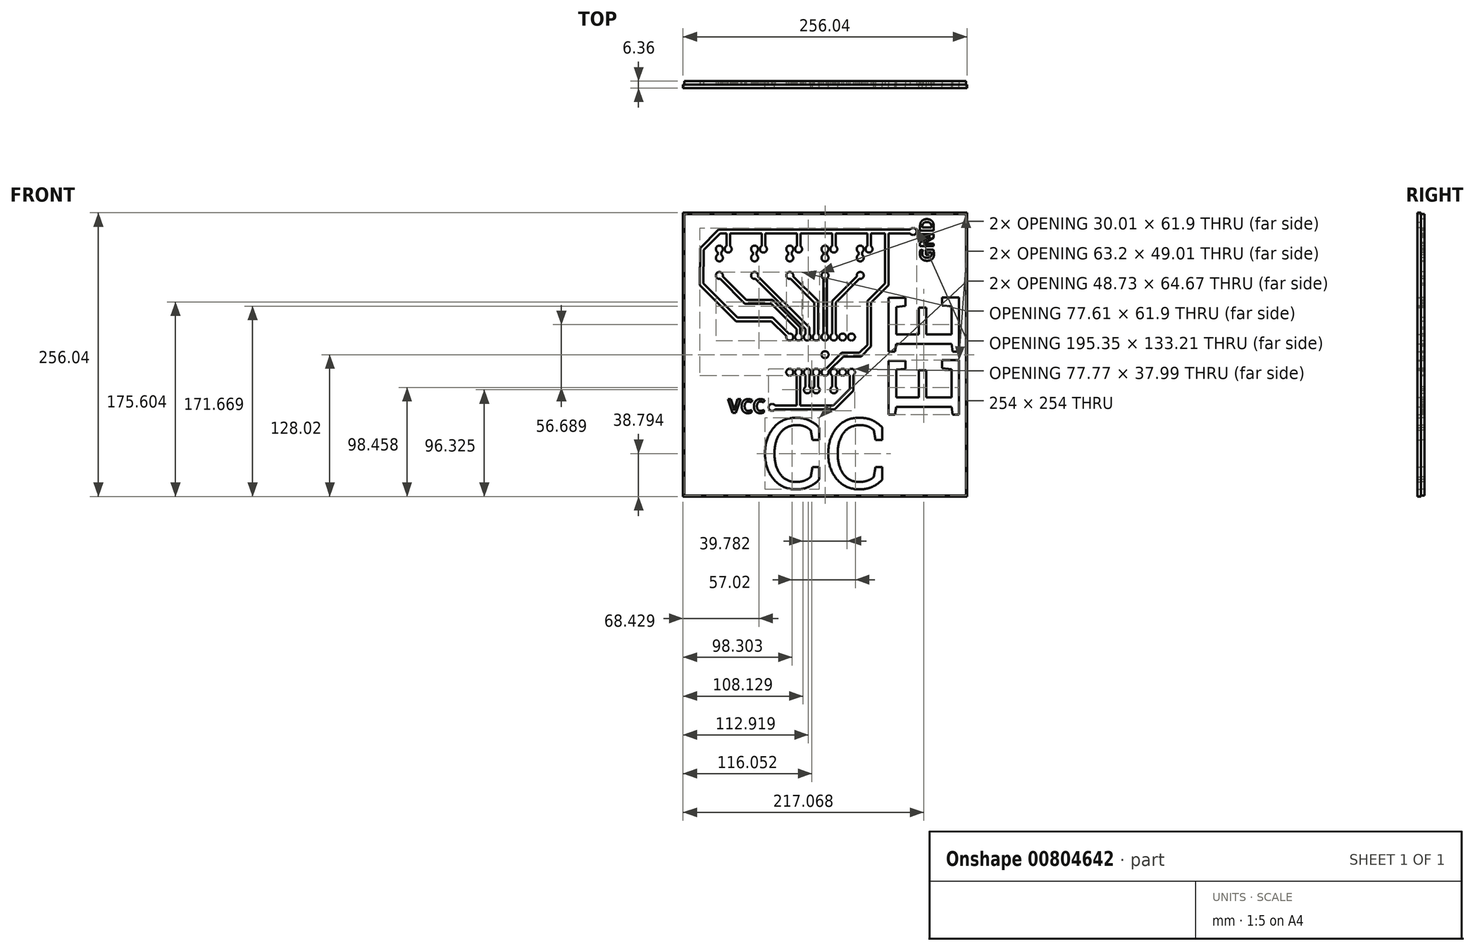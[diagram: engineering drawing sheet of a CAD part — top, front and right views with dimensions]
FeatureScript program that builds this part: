
annotation { "Feature Type Name" : "Feature", "Feature Type Description" : "" }
export const myFeature = defineFeature(function(context is Context, id is Id, definition is map)
    precondition{}
    {
        {
            var Q0;
            Q0=qCreatedBy(makeId("Front.planeOp"),FACE);
            var sketch = newSketch(context, id + "F0", { "sketchPlane" : qUnion([Q0])});
            skLineSegment(sketch, "E0.bottom", {"start": v(127, 127) * mm, "end": v(-127, 127) * mm});
            skLineSegment(sketch, "E0.top", {"start": v(127, -127) * mm, "end": v(-127, -127) * mm});
            skLineSegment(sketch, "E0.left", {"start": v(127, 127) * mm, "end": v(127, -127) * mm});
            skLineSegment(sketch, "E0.right", {"start": v(-127, 127) * mm, "end": v(-127, -127) * mm});
            skPoint(sketch, "E0.middle", {"position": v(0, 0) * mm});
            skText(sketch, "E1", { "text": "CC", "fontName": "RobotoSlab-Regular.ttf"});
            skText(sketch, "E2", { "text": "EE", "fontName": "RobotoSlab-Regular.ttf"});
            skText(sketch, "E3", { "text": "TOP", "fontName": "OpenSans-Regular.ttf"});
            skCircle(sketch, "E4", {"center": v(0, 0) * mm, "radius": 3.18 * mm});
            skLineSegment(sketch, "E5.0", {"start": v(128.02, -128.02) * mm, "end": v(-128.02, -128.02) * mm});
            skLineSegment(sketch, "E5.1", {"start": v(128.02, 128.02) * mm, "end": v(128.02, -128.02) * mm});
            skLineSegment(sketch, "E5.2", {"start": v(128.02, 128.02) * mm, "end": v(-128.02, 128.02) * mm});
            skLineSegment(sketch, "E5.3", {"start": v(-128.02, 128.02) * mm, "end": v(-128.02, -128.02) * mm});
            skPoint(sketch, "E6", {"position": v(0, 15.88) * mm});
            skPoint(sketch, "E7", {"position": v(0, -15.88) * mm});
            skPoint(sketch, "E8", {"position": v(7.95, -15.88) * mm});
            skPoint(sketch, "E9", {"position": v(15.9, -15.88) * mm});
            skPoint(sketch, "E10", {"position": v(23.85, -15.88) * mm});
            skPoint(sketch, "E11", {"position": v(-7.95, -15.88) * mm});
            skPoint(sketch, "E12", {"position": v(-15.9, -15.88) * mm});
            skPoint(sketch, "E13", {"position": v(-23.85, -15.88) * mm});
            skPoint(sketch, "E14", {"position": v(-31.8, -15.88) * mm});
            skPoint(sketch, "E15", {"position": v(7.95, 15.88) * mm});
            skPoint(sketch, "E16", {"position": v(15.9, 15.88) * mm});
            skPoint(sketch, "E17", {"position": v(23.85, 15.88) * mm});
            skPoint(sketch, "E18", {"position": v(-7.95, 15.88) * mm});
            skPoint(sketch, "E19", {"position": v(-15.9, 15.88) * mm});
            skPoint(sketch, "E20", {"position": v(-23.85, 15.88) * mm});
            skPoint(sketch, "E21", {"position": v(-31.8, 15.88) * mm});
            skPoint(sketch, "E22", {"position": v(-15.9, -31.75) * mm});
            skPoint(sketch, "E23", {"position": v(-7.95, -31.75) * mm});
            skPoint(sketch, "E24", {"position": v(7.95, -31.75) * mm});
            skPoint(sketch, "E25", {"position": v(-47.68, -47.62) * mm});
            skPoint(sketch, "E26", {"position": v(0, 71.45) * mm});
            skPoint(sketch, "E27", {"position": v(31.75, 71.45) * mm});
            skPoint(sketch, "E28", {"position": v(-31.75, 71.45) * mm});
            skPoint(sketch, "E29", {"position": v(-63.5, 71.45) * mm});
            skPoint(sketch, "E30", {"position": v(-95.25, 71.45) * mm});
            skArc(sketch, "E31", {"start": v(-34.87, 16.68) * mm, "mid": v(-29.56, 13.63) * mm, "end": v(-32.6, 18.95) * mm});
            skArc(sketch, "E32", {"start": v(-24.98, 18.84) * mm, "mid": v(-24.11, 12.71) * mm, "end": v(-22.25, 18.62) * mm});
            skArc(sketch, "E33", {"start": v(-17.5, 18.62) * mm, "mid": v(-15.9, 12.7) * mm, "end": v(-14.3, 18.62) * mm});
            skArc(sketch, "E34", {"start": v(-9.55, 18.62) * mm, "mid": v(-7.95, 12.7) * mm, "end": v(-6.35, 18.62) * mm});
            skArc(sketch, "E35", {"start": v(-1.6, 18.62) * mm, "mid": v(0, 12.7) * mm, "end": v(1.6, 18.62) * mm});
            skArc(sketch, "E36", {"start": v(6.35, 18.62) * mm, "mid": v(7.95, 12.7) * mm, "end": v(9.55, 18.62) * mm});
            skCircle(sketch, "E37", {"center": v(15.9, 15.88) * mm, "radius": 3.18 * mm});
            skCircle(sketch, "E38", {"center": v(23.85, 15.88) * mm, "radius": 3.18 * mm});
            skCircle(sketch, "E39", {"center": v(-31.8, -15.88) * mm, "radius": 3.18 * mm});
            skArc(sketch, "E40", {"start": v(-22.25, -18.62) * mm, "mid": v(-24.68, -12.81) * mm, "end": v(-23.85, -19.05) * mm});
            skArc(sketch, "E41", {"start": v(-15.9, -19.05) * mm, "mid": v(-15.07, -12.81) * mm, "end": v(-17.5, -18.62) * mm});
            skArc(sketch, "E42", {"start": v(-6.35, -18.62) * mm, "mid": v(-7.95, -12.7) * mm, "end": v(-9.55, -18.62) * mm});
            skArc(sketch, "E43", {"start": v(0.8, -12.8) * mm, "mid": v(-2.24, -18.12) * mm, "end": v(3.07, -15.07) * mm});
            skArc(sketch, "E44", {"start": v(9.55, -18.62) * mm, "mid": v(7.95, -12.7) * mm, "end": v(6.35, -18.62) * mm});
            skCircle(sketch, "E45", {"center": v(15.9, -15.88) * mm, "radius": 3.18 * mm});
            skArc(sketch, "E46", {"start": v(25.45, -18.62) * mm, "mid": v(23.85, -12.7) * mm, "end": v(22.25, -18.62) * mm});
            skArc(sketch, "E47", {"start": v(30.94, 68.38) * mm, "mid": v(34, 73.7) * mm, "end": v(28.68, 70.64) * mm});
            skArc(sketch, "E48", {"start": v(1.6, 68.7) * mm, "mid": v(0, 74.63) * mm, "end": v(-1.6, 68.7) * mm});
            skArc(sketch, "E49", {"start": v(-28.68, 70.64) * mm, "mid": v(-34, 73.7) * mm, "end": v(-30.94, 68.38) * mm});
            skArc(sketch, "E50", {"start": v(-60.43, 70.64) * mm, "mid": v(-65.74, 73.7) * mm, "end": v(-62.7, 68.38) * mm});
            skArc(sketch, "E51", {"start": v(-92.18, 70.64) * mm, "mid": v(-97.5, 73.7) * mm, "end": v(-94.45, 68.38) * mm});
            skPoint(sketch, "E52", {"position": v(7.95, 47.62) * mm});
            skPoint(sketch, "E53", {"position": v(-7.95, 47.62) * mm});
            skPoint(sketch, "E54", {"position": v(-15.9, 23.83) * mm});
            skPoint(sketch, "E55", {"position": v(-23.85, 23.83) * mm});
            skPoint(sketch, "E56", {"position": v(-47.68, 47.62) * mm});
            skPoint(sketch, "E57", {"position": v(-71.5, 47.62) * mm});
            skPoint(sketch, "E58", {"position": v(-47.68, 31.75) * mm});
            skPoint(sketch, "E59", {"position": v(-79.43, 31.75) * mm});
            skPoint(sketch, "E60", {"position": v(-111.12, 95.25) * mm});
            skPoint(sketch, "E61", {"position": v(-111.18, 63.5) * mm});
            skPoint(sketch, "E62", {"position": v(-95.25, 95.25) * mm});
            skPoint(sketch, "E63", {"position": v(-87.3, 95.25) * mm});
            skPoint(sketch, "E64", {"position": v(-63.5, 95.25) * mm});
            skPoint(sketch, "E65", {"position": v(-55.55, 95.25) * mm});
            skPoint(sketch, "E66", {"position": v(-31.75, 95.25) * mm});
            skPoint(sketch, "E67", {"position": v(-23.8, 95.25) * mm});
            skPoint(sketch, "E68", {"position": v(0, 95.25) * mm});
            skPoint(sketch, "E69", {"position": v(31.75, 95.25) * mm});
            skPoint(sketch, "E70", {"position": v(7.95, 95.25) * mm});
            skPoint(sketch, "E71", {"position": v(39.7, 95.25) * mm});
            skPoint(sketch, "E72", {"position": v(-95.25, 87.3) * mm});
            skPoint(sketch, "E73", {"position": v(-63.5, 87.3) * mm});
            skPoint(sketch, "E74", {"position": v(-31.75, 87.3) * mm});
            skPoint(sketch, "E75", {"position": v(0, 87.3) * mm});
            skPoint(sketch, "E76", {"position": v(31.75, 87.3) * mm});
            skPoint(sketch, "E77", {"position": v(-95.25, 111.12) * mm});
            skPoint(sketch, "E78", {"position": v(55.58, 111.12) * mm});
            skArc(sketch, "E79", {"start": v(-96.85, 90.04) * mm, "mid": v(-95.25, 84.12) * mm, "end": v(-93.65, 90.04) * mm});
            skArc(sketch, "E80", {"start": v(-93.65, 92.5) * mm, "mid": v(-95.25, 98.42) * mm, "end": v(-96.85, 92.5) * mm});
            skArc(sketch, "E81", {"start": v(-88.9, 98) * mm, "mid": v(-87.3, 92.07) * mm, "end": v(-85.7, 98) * mm});
            skArc(sketch, "E82", {"start": v(-61.9, 92.5) * mm, "mid": v(-63.5, 98.42) * mm, "end": v(-65.1, 92.5) * mm});
            skArc(sketch, "E83", {"start": v(-65.1, 90.04) * mm, "mid": v(-63.5, 84.12) * mm, "end": v(-61.9, 90.04) * mm});
            skArc(sketch, "E84", {"start": v(-33.35, 90.04) * mm, "mid": v(-31.75, 84.12) * mm, "end": v(-30.15, 90.04) * mm});
            skArc(sketch, "E85", {"start": v(-57.15, 98) * mm, "mid": v(-55.55, 92.07) * mm, "end": v(-53.95, 98) * mm});
            skArc(sketch, "E86", {"start": v(-30.15, 92.5) * mm, "mid": v(-31.75, 98.42) * mm, "end": v(-33.35, 92.5) * mm});
            skArc(sketch, "E87", {"start": v(-25.4, 98) * mm, "mid": v(-23.8, 92.07) * mm, "end": v(-22.2, 98) * mm});
            skArc(sketch, "E88", {"start": v(-1.6, 90.04) * mm, "mid": v(0, 84.12) * mm, "end": v(1.6, 90.04) * mm});
            skArc(sketch, "E89", {"start": v(1.6, 92.5) * mm, "mid": v(0, 98.42) * mm, "end": v(-1.6, 92.5) * mm});
            skArc(sketch, "E90", {"start": v(6.35, 98) * mm, "mid": v(7.95, 92.07) * mm, "end": v(9.55, 98) * mm});
            skArc(sketch, "E91", {"start": v(30.15, 90.04) * mm, "mid": v(31.75, 84.12) * mm, "end": v(33.35, 90.04) * mm});
            skArc(sketch, "E92", {"start": v(33.35, 92.5) * mm, "mid": v(31.75, 98.42) * mm, "end": v(30.15, 92.5) * mm});
            skArc(sketch, "E93", {"start": v(38.1, 98) * mm, "mid": v(39.7, 92.07) * mm, "end": v(41.3, 98) * mm});
            skArc(sketch, "E94", {"start": v(76.66, 109.52) * mm, "mid": v(82.58, 111.12) * mm, "end": v(76.66, 112.73) * mm});
            skArc(sketch, "E95", {"start": v(6.35, -29) * mm, "mid": v(7.95, -34.92) * mm, "end": v(9.55, -29) * mm});
            skArc(sketch, "E96", {"start": v(-7.95, -28.57) * mm, "mid": v(-8.78, -34.81) * mm, "end": v(-6.35, -29) * mm});
            skArc(sketch, "E97", {"start": v(-17.5, -29) * mm, "mid": v(-15.9, -34.92) * mm, "end": v(-14.3, -29) * mm});
            skPoint(sketch, "E98", {"position": v(7.95, -47.62) * mm});
            skPoint(sketch, "E99", {"position": v(23.85, -31.75) * mm});
            skLineSegment(sketch, "E100.0", {"start": v(-95.91, 112.73) * mm, "end": v(79.4, 112.73) * mm});
            skLineSegment(sketch, "E100.1", {"start": v(-95.91, 112.73) * mm, "end": v(-112.72, 95.91) * mm});
            skLineSegment(sketch, "E100.2", {"start": v(-32.93, 14.74) * mm, "end": v(-48.34, 30.15) * mm});
            skLineSegment(sketch, "E100.3", {"start": v(-48.34, 30.15) * mm, "end": v(-80.09, 30.15) * mm});
            skLineSegment(sketch, "E100.4", {"start": v(-80.09, 30.15) * mm, "end": v(-112.78, 62.84) * mm});
            skLineSegment(sketch, "E100.5", {"start": v(-112.78, 62.84) * mm, "end": v(-112.72, 95.91) * mm});
            skLineSegment(sketch, "E101.0", {"start": v(-72.17, 46.02) * mm, "end": v(-96.38, 70.32) * mm});
            skLineSegment(sketch, "E101.1", {"start": v(-48.34, 46.02) * mm, "end": v(-72.17, 46.02) * mm});
            skLineSegment(sketch, "E101.2", {"start": v(-24.98, 22.7) * mm, "end": v(-48.34, 46.02) * mm});
            skLineSegment(sketch, "E102.0", {"start": v(-17.5, 23.16) * mm, "end": v(-64.63, 70.32) * mm});
            skLineSegment(sketch, "E102.1", {"start": v(-17.5, 15.88) * mm, "end": v(-17.5, 23.16) * mm});
            skLineSegment(sketch, "E103.0", {"start": v(-14.3, 24.49) * mm, "end": v(-62.37, 72.58) * mm});
            skLineSegment(sketch, "E103.1", {"start": v(-14.3, 15.87) * mm, "end": v(-14.3, 24.49) * mm});
            skLineSegment(sketch, "E104.0", {"start": v(-70.84, 49.23) * mm, "end": v(-94.12, 72.58) * mm});
            skLineSegment(sketch, "E104.1", {"start": v(-47.01, 49.23) * mm, "end": v(-70.84, 49.23) * mm});
            skLineSegment(sketch, "E104.2", {"start": v(-22.25, 24.49) * mm, "end": v(-47.01, 49.23) * mm});
            skLineSegment(sketch, "E104.3", {"start": v(-22.25, 24.49) * mm, "end": v(-22.25, 15.88) * mm});
            skLineSegment(sketch, "E105.0", {"start": v(-94.59, 109.52) * mm, "end": v(-88.9, 109.52) * mm});
            skLineSegment(sketch, "E105.1", {"start": v(-94.59, 109.52) * mm, "end": v(-109.53, 94.59) * mm});
            skLineSegment(sketch, "E105.2", {"start": v(-30.67, 17) * mm, "end": v(-47.01, 33.35) * mm});
            skLineSegment(sketch, "E105.3", {"start": v(-47.01, 33.35) * mm, "end": v(-78.76, 33.35) * mm});
            skLineSegment(sketch, "E105.4", {"start": v(-78.76, 33.35) * mm, "end": v(-109.57, 64.16) * mm});
            skLineSegment(sketch, "E105.5", {"start": v(-109.57, 64.16) * mm, "end": v(-109.53, 94.59) * mm});
            skLineSegment(sketch, "E106.0", {"start": v(1.13, -17) * mm, "end": v(16.52, -1.6) * mm});
            skLineSegment(sketch, "E106.1", {"start": v(16.52, -1.6) * mm, "end": v(32.4, -1.6) * mm});
            skLineSegment(sketch, "E106.2", {"start": v(57.18, 111.12) * mm, "end": v(57.18, 62.84) * mm});
            skLineSegment(sketch, "E106.3", {"start": v(57.18, 62.84) * mm, "end": v(41.3, 46.95) * mm});
            skLineSegment(sketch, "E106.4", {"start": v(41.3, 46.95) * mm, "end": v(41.3, 7.31) * mm});
            skLineSegment(sketch, "E106.5", {"start": v(32.4, -1.6) * mm, "end": v(41.3, 7.31) * mm});
            skLineSegment(sketch, "E107.0", {"start": v(-1.13, -14.74) * mm, "end": v(15.2, 1.6) * mm});
            skLineSegment(sketch, "E107.1", {"start": v(15.2, 1.6) * mm, "end": v(31.07, 1.6) * mm});
            skLineSegment(sketch, "E107.2", {"start": v(53.97, 111.12) * mm, "end": v(53.97, 64.16) * mm});
            skLineSegment(sketch, "E107.3", {"start": v(53.97, 64.16) * mm, "end": v(38.1, 48.27) * mm});
            skLineSegment(sketch, "E107.4", {"start": v(38.1, 48.27) * mm, "end": v(38.1, 8.64) * mm});
            skLineSegment(sketch, "E107.5", {"start": v(31.07, 1.6) * mm, "end": v(38.1, 8.64) * mm});
            skLineSegment(sketch, "E108.0", {"start": v(38.1, 95.25) * mm, "end": v(38.1, 111.12) * mm});
            skLineSegment(sketch, "E109.0", {"start": v(41.3, 95.25) * mm, "end": v(41.3, 111.12) * mm});
            skLineSegment(sketch, "E110.0", {"start": v(9.55, 95.25) * mm, "end": v(9.55, 111.12) * mm});
            skLineSegment(sketch, "E111.0", {"start": v(6.35, 95.25) * mm, "end": v(6.35, 111.12) * mm});
            skLineSegment(sketch, "E112.0", {"start": v(1.6, 95.25) * mm, "end": v(1.6, 87.3) * mm});
            skLineSegment(sketch, "E113.0", {"start": v(-1.6, 95.25) * mm, "end": v(-1.6, 87.3) * mm});
            skLineSegment(sketch, "E114.0", {"start": v(-22.2, 95.25) * mm, "end": v(-22.2, 111.12) * mm});
            skLineSegment(sketch, "E115.0", {"start": v(-25.4, 95.25) * mm, "end": v(-25.4, 111.12) * mm});
            skLineSegment(sketch, "E116.0", {"start": v(-53.95, 95.25) * mm, "end": v(-53.95, 111.12) * mm});
            skLineSegment(sketch, "E117.0", {"start": v(-85.7, 95.25) * mm, "end": v(-85.7, 111.12) * mm});
            skLineSegment(sketch, "E118.0", {"start": v(-57.15, 95.25) * mm, "end": v(-57.15, 111.12) * mm});
            skLineSegment(sketch, "E119.0", {"start": v(-30.15, 87.3) * mm, "end": v(-30.15, 95.25) * mm});
            skLineSegment(sketch, "E120.0", {"start": v(-33.35, 87.3) * mm, "end": v(-33.35, 95.25) * mm});
            skLineSegment(sketch, "E121.0", {"start": v(-88.9, 95.25) * mm, "end": v(-88.9, 111.12) * mm});
            skLineSegment(sketch, "E122.0", {"start": v(-9.55, 46.96) * mm, "end": v(-32.88, 70.32) * mm});
            skLineSegment(sketch, "E122.1", {"start": v(-9.55, 46.96) * mm, "end": v(-9.55, 15.88) * mm});
            skLineSegment(sketch, "E123.0", {"start": v(-6.35, 48.29) * mm, "end": v(-30.62, 72.58) * mm});
            skLineSegment(sketch, "E123.1", {"start": v(-6.35, 48.29) * mm, "end": v(-6.35, 15.88) * mm});
            skLineSegment(sketch, "E124.0", {"start": v(1.6, 19.05) * mm, "end": v(1.6, 68.28) * mm});
            skLineSegment(sketch, "E125.0", {"start": v(-1.6, 19.05) * mm, "end": v(-1.6, 68.28) * mm});
            skLineSegment(sketch, "E126.0", {"start": v(9.55, 46.96) * mm, "end": v(9.55, 15.88) * mm});
            skLineSegment(sketch, "E126.1", {"start": v(9.55, 46.96) * mm, "end": v(32.88, 70.32) * mm});
            skLineSegment(sketch, "E127.0", {"start": v(6.35, 48.29) * mm, "end": v(30.62, 72.58) * mm});
            skLineSegment(sketch, "E127.1", {"start": v(6.35, 48.29) * mm, "end": v(6.35, 15.88) * mm});
            skLineSegment(sketch, "E128", {"start": v(1.6, 68.28) * mm, "end": v(1.6, 68.7) * mm});
            skLineSegment(sketch, "E129", {"start": v(-1.6, 68.28) * mm, "end": v(-1.6, 68.7) * mm});
            skLineSegment(sketch, "E130", {"start": v(-1.6, 19.05) * mm, "end": v(-1.6, 18.62) * mm});
            skLineSegment(sketch, "E131", {"start": v(1.6, 19.05) * mm, "end": v(1.6, 18.62) * mm});
            skLineSegment(sketch, "E132.0", {"start": v(-47.68, -49.23) * mm, "end": v(8.61, -49.23) * mm});
            skLineSegment(sketch, "E132.1", {"start": v(25.45, -32.41) * mm, "end": v(8.61, -49.23) * mm});
            skLineSegment(sketch, "E132.2", {"start": v(25.45, -15.88) * mm, "end": v(25.45, -32.41) * mm});
            skLineSegment(sketch, "E133.0", {"start": v(-47.68, -46.02) * mm, "end": v(-25.45, -46.02) * mm});
            skLineSegment(sketch, "E133.1", {"start": v(22.25, -31.09) * mm, "end": v(7.29, -46.02) * mm});
            skLineSegment(sketch, "E133.2", {"start": v(22.25, -15.88) * mm, "end": v(22.25, -31.09) * mm});
            skArc(sketch, "E134", {"start": v(-44.93, -46.02) * mm, "mid": v(-50.85, -47.62) * mm, "end": v(-44.93, -49.23) * mm});
            skLineSegment(sketch, "E135.0", {"start": v(6.35, -15.88) * mm, "end": v(6.35, -31.75) * mm});
            skLineSegment(sketch, "E136.0", {"start": v(9.55, -15.88) * mm, "end": v(9.55, -31.75) * mm});
            skLineSegment(sketch, "E137.0", {"start": v(-25.45, -15.88) * mm, "end": v(-25.45, -47.62) * mm});
            skLineSegment(sketch, "E138.0", {"start": v(-22.25, -15.88) * mm, "end": v(-22.25, -47.62) * mm});
            skLineSegment(sketch, "E139.0", {"start": v(-14.3, -15.88) * mm, "end": v(-14.3, -31.75) * mm});
            skLineSegment(sketch, "E140.0", {"start": v(-17.5, -15.88) * mm, "end": v(-17.5, -31.75) * mm});
            skLineSegment(sketch, "E141.0", {"start": v(-6.35, -15.88) * mm, "end": v(-6.35, -31.75) * mm});
            skLineSegment(sketch, "E142.0", {"start": v(-9.55, -15.88) * mm, "end": v(-9.55, -31.75) * mm});
            skLineSegment(sketch, "E143.0", {"start": v(33.35, 87.3) * mm, "end": v(33.35, 95.25) * mm});
            skLineSegment(sketch, "E144.0", {"start": v(30.15, 87.3) * mm, "end": v(30.15, 95.25) * mm});
            skLineSegment(sketch, "E145.0", {"start": v(-96.85, 87.3) * mm, "end": v(-96.85, 95.25) * mm});
            skLineSegment(sketch, "E146.0", {"start": v(-93.65, 87.3) * mm, "end": v(-93.65, 95.25) * mm});
            skLineSegment(sketch, "E147.0", {"start": v(-61.9, 95.25) * mm, "end": v(-61.9, 87.3) * mm});
            skLineSegment(sketch, "E148.0", {"start": v(-65.1, 95.25) * mm, "end": v(-65.1, 87.3) * mm});
            skLineSegment(sketch, "E149.trimOffspring", {"start": v(-22.25, -46.02) * mm, "end": v(7.29, -46.02) * mm});
            skLineSegment(sketch, "E150.trimOffspring", {"start": v(57.18, 109.52) * mm, "end": v(79.4, 109.52) * mm});
            skLineSegment(sketch, "E151.trimOffspring", {"start": v(41.3, 109.52) * mm, "end": v(53.97, 109.52) * mm});
            skLineSegment(sketch, "E152.trimOffspring", {"start": v(-85.7, 109.52) * mm, "end": v(-57.15, 109.52) * mm});
            skLineSegment(sketch, "E153.trimOffspring", {"start": v(-53.95, 109.52) * mm, "end": v(-25.4, 109.52) * mm});
            skLineSegment(sketch, "E154.trimOffspring", {"start": v(-22.2, 109.52) * mm, "end": v(6.35, 109.52) * mm});
            skLineSegment(sketch, "E155.trimOffspring", {"start": v(9.55, 109.52) * mm, "end": v(38.1, 109.52) * mm});
            skLineSegment(sketch, "E156.0", {"start": v(-25.45, 23.83) * mm, "end": v(-25.45, 15.87) * mm});
            skText(sketch, "E157", { "text": "VCC", "fontName": "OpenSans-Bold.ttf"});
            skText(sketch, "E158", { "text": "GND", "fontName": "OpenSans-Bold.ttf"});
            const initialGuessF0  = {"E1": [-0.05715, -0.12065, 1, 0, 0.06365], "E2": [0.12065, -0.05715, 0, 1, 0.06401], "E3": [-0.3062, 0.1728, 1, 0, 0.06138], "E157": [-0.08746, -0.05266, 1, 0, 0.01252], "E158": [0.09807, 0.08372, 0, 1, 0.01252]};
            skSetInitialGuess(sketch, initialGuessF0);
            skSolve(sketch);
        }
        {
            var Q0;
            Q0=makeQuery(id+"F0.imprint","IMPRINT",FACE,{"disambiguationData":[TD([[makeQuery(id+"F0.imprint","IMPRINT",EDGE,{"derivedFrom":sQuery(id+"F0.wireOp",EDGE,"E1.sketch_text.stroke-24")}),-1.0]])]});
            var Q1;
            Q1=makeQuery(id+"F0.imprint","IMPRINT",FACE,{"disambiguationData":[TD([[makeQuery(id+"F0.imprint","IMPRINT",EDGE,{"derivedFrom":sQuery(id+"F0.wireOp",EDGE,"E1.sketch_text.stroke-0")}),-1.0]])]});
            var Q2;
            Q2=makeQuery(id+"F0.imprint","IMPRINT",FACE,{"disambiguationData":[TD([[makeQuery(id+"F0.imprint","IMPRINT",EDGE,{"derivedFrom":sQuery(id+"F0.wireOp",EDGE,"E2.sketch_text.stroke-0")}),-1.0]])]});
            var Q3;
            Q3=makeQuery(id+"F0.imprint","IMPRINT",FACE,{"disambiguationData":[TD([[makeQuery(id+"F0.imprint","IMPRINT",EDGE,{"derivedFrom":sQuery(id+"F0.wireOp",EDGE,"E2.sketch_text.stroke-20")}),-1.0]])]});
            var Q4;
            Q4=makeQuery(id+"F0.imprint","IMPRINT",FACE,{"disambiguationData":[TD([[makeQuery(id+"F0.imprint","IMPRINT",EDGE,{"derivedFrom":sQuery(id+"F0.wireOp",EDGE,"E0.bottom")}),-1.0]])]});
            var Q5;
            Q5=makeQuery(id+"F0.imprint","IMPRINT",FACE,{"disambiguationData":[TD([[makeQuery(id+"F0.imprint","IMPRINT",EDGE,{"derivedFrom":sQuery(id+"F0.wireOp",EDGE,"E158.sketch_text.stroke-40")}),1.0]])]});
            extrude(context, id + "F1", {"entities" : qUnion([Q0, Q1, Q2, Q3, Q4, Q5]), "depth" : 3.17 * mm, "offsetDistance" : 25.4 * mm});
        }
        {
            var Q0;
            Q0=makeQuery(id+"F0.imprint","IMPRINT",FACE,{"disambiguationData":[TD([[makeQuery(id+"F0.imprint","IMPRINT",EDGE,{"derivedFrom":sQuery(id+"F0.wireOp",EDGE,"E0.bottom")}),1.0]])]});
            extrude(context, id + "F2", {"entities" : qUnion([Q0]), "oppositeDirection" : true, "depth" : 3.17 * mm, "offsetDistance" : 25.4 * mm});
        }
    });
